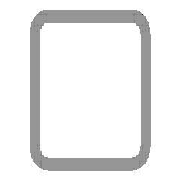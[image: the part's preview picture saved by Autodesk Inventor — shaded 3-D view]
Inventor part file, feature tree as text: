
AUTODESK INVENTOR PART (.ipt)
format: ipt  version: 2021 (Build 250183000, 183)  size: 140,288 bytes
history: native  units: mm (DEFAULTED — no unit token found)
features: other x5, sketch x3, extrude x1, split x1, plane x1
ambient origin geometry x8: Origin, YZ Plane, XZ Plane, XY Plane, X Axis, Y Axis, Z Axis, Center Point
bodies: Solid1 (feature_tree)
feature tree (11):
  parser-record x1  (decoder bookkeeping rows leaked as tree rows — omitted from the tree; the rows remain in map.json)
  other  "Driven Length"
  other  "Plano inicial"
  other  "Plano final"
  extrude  "Corpo"  TaperAngle=0.0deg  [1 undecoded]
  other  "Plano de trabalho4"
  split  "Dividir1"
  sketch  "Esboço"  dims[d11=50.8mm d12=4.7625mm d13=-0.0mm d14=1019.555514mm d15=25.4mm d16=25.4mm d17=9.525mm d18=90.0deg d19=1019.555514mm]
  sketch  "Sketch3"  dims[d3=1017.407634mm d4=0.0mm]
  plane  "Work Plane3"
  sketch  "Sketch4"  dims[d10=50.8mm]
note: 1 required parameter value undecoded (feature->parameter linkage not recoverable at this tier; creation-order binding heuristic only, values carry confidence <= 0.55)
